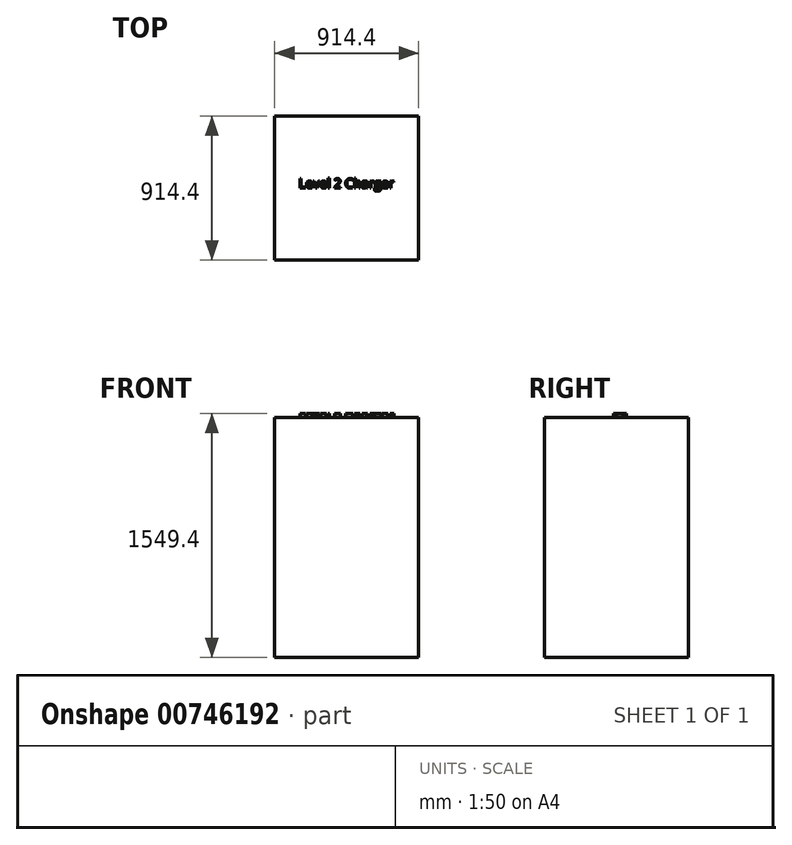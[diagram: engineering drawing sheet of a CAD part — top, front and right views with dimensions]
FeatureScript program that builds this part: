
annotation { "Feature Type Name" : "Feature", "Feature Type Description" : "" }
export const myFeature = defineFeature(function(context is Context, id is Id, definition is map)
    precondition{}
    {
        {
            var Q0;
            Q0=qCreatedBy(makeId("Top.planeOp"),FACE);
            var sketch = newSketch(context, id + "F0", { "sketchPlane" : qUnion([Q0])});
            skLineSegment(sketch, "E0.bottom", {"start": v(457.2, -457.2) * mm, "end": v(-457.2, -457.2) * mm});
            skLineSegment(sketch, "E0.top", {"start": v(457.2, 457.2) * mm, "end": v(-457.2, 457.2) * mm});
            skLineSegment(sketch, "E0.left", {"start": v(457.2, -457.2) * mm, "end": v(457.2, 457.2) * mm});
            skLineSegment(sketch, "E0.right", {"start": v(-457.2, -457.2) * mm, "end": v(-457.2, 457.2) * mm});
            skPoint(sketch, "E0.middle", {"position": v(0, 0) * mm});
            skSolve(sketch);
        }
        {
            var Q0;
            Q0 = qSketchRegion(id + "F0", true);
            extrude(context, id + "F1", {"entities" : qUnion([Q0]), "depth" : 1524 * mm, "offsetDistance" : 30.48 * mm});
        }
        {
            var Q0;
            Q0=makeQuery(id+"F1.opExtrude","CAP_FACE",FACE,{"disambiguationData":[OSD([sQuery(id+"F0.wireOp",EDGE,"E0.bottom"),sQuery(id+"F0.wireOp",EDGE,"E0.top"),sQuery(id+"F0.wireOp",EDGE,"E0.left"),sQuery(id+"F0.wireOp",EDGE,"E0.right")])],"isStart":false});
            var sketch = newSketch(context, id + "F2", { "sketchPlane" : qUnion([Q0])});
            skText(sketch, "E1", { "text": "Level 2 Charger", "fontName": "OpenSans-Regular.ttf"});
            const initialGuessF2  = {"E1": [-0.3048, 0, 1, 0, 0.06043]};
            skSetInitialGuess(sketch, initialGuessF2);
            skSolve(sketch);
        }
        {
            var Q0;
            Q0 = qSketchRegion(id + "F2", true);
            extrude(context, id + "F3", {"entities" : qUnion([Q0]), "operationType" : NewBodyOperationType.ADD, "depth" : 25.4 * mm, "offsetDistance" : 30.48 * mm});
        }
    });
